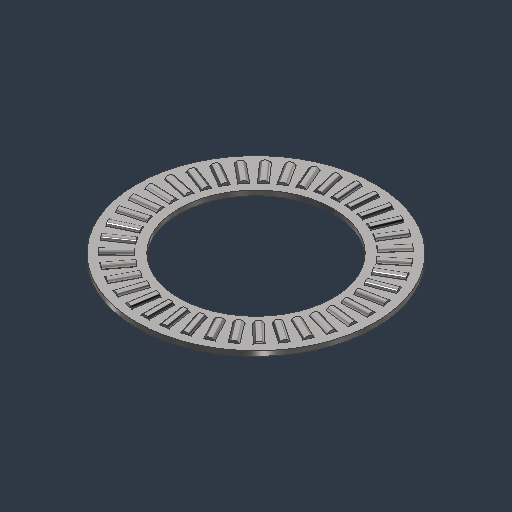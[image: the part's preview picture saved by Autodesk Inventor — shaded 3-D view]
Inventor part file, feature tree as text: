
AUTODESK INVENTOR PART (.ipt)
format: ipt  version: 2024.3 (Build 283343000, 343)  size: 479,232 bytes
history: native  units: mm (DEFAULTED — no unit token found)
features: other x38, revolve x1, pattern_circular x1
ambient origin geometry x8: Origin, YZ Plane, XZ Plane, XY Plane, X Axis, Y Axis, Z Axis, Center Point
bodies: Solid1 (feature_tree), Solid2 (feature_tree), Solid3 (feature_tree), Solid4 (feature_tree), Solid5 (feature_tree), Solid6 (feature_tree), Solid7 (feature_tree), Solid8 (feature_tree), Solid9 (feature_tree), Solid10 (feature_tree), Solid11 (feature_tree), Solid12 (feature_tree), Solid13 (feature_tree), Solid14 (feature_tree), Solid15 (feature_tree), Solid16 (feature_tree), Solid17 (feature_tree), Solid18 (feature_tree), Solid19 (feature_tree), Solid20 (feature_tree), Solid21 (feature_tree), Solid22 (feature_tree), Solid23 (feature_tree), Solid24 (feature_tree), Solid25 (feature_tree), Solid26 (feature_tree), Solid27 (feature_tree), Solid28 (feature_tree), Solid29 (feature_tree), Solid30 (feature_tree), Solid31 (feature_tree), Solid32 (feature_tree), Solid33 (feature_tree), Solid34 (feature_tree), Solid35 (feature_tree), Solid36 (feature_tree), Solid37 (feature_tree), Solid38 (feature_tree), Solid39 (feature_tree), Solid40 (feature_tree)
feature tree (40):
  revolve  "Revolve2"  [1 undecoded]
  other  "CirPattern1[1]"
  other  "CirPattern1[2]"
  other  "CirPattern1[3]"
  other  "CirPattern1[4]"
  other  "CirPattern1[5]"
  other  "CirPattern1[6]"
  other  "CirPattern1[7]"
  other  "CirPattern1[8]"
  other  "CirPattern1[9]"
  other  "CirPattern1[10]"
  other  "CirPattern1[11]"
  other  "CirPattern1[12]"
  other  "CirPattern1[13]"
  other  "CirPattern1[14]"
  other  "CirPattern1[15]"
  other  "CirPattern1[16]"
  other  "CirPattern1[17]"
  other  "CirPattern1[18]"
  other  "CirPattern1[19]"
  other  "CirPattern1[20]"
  pattern_circular  "CirPattern2"
  other  "CirPattern1[21]"
  other  "CirPattern1[22]"
  other  "CirPattern1[23]"
  other  "CirPattern1[24]"
  other  "CirPattern1[25]"
  other  "CirPattern1[26]"
  other  "CirPattern1[27]"
  other  "CirPattern1[28]"
  other  "CirPattern1[29]"
  other  "CirPattern1[30]"
  other  "CirPattern1[31]"
  other  "CirPattern1[32]"
  other  "CirPattern1[33]"
  other  "CirPattern1[34]"
  other  "CirPattern1[35]"
  other  "CirPattern1[36]"
  other  "CirPattern1[37]"
  other  "CirPattern1[38]"
note: 1 required parameter value undecoded (feature->parameter linkage not recoverable at this tier; creation-order binding heuristic only, values carry confidence <= 0.55)
